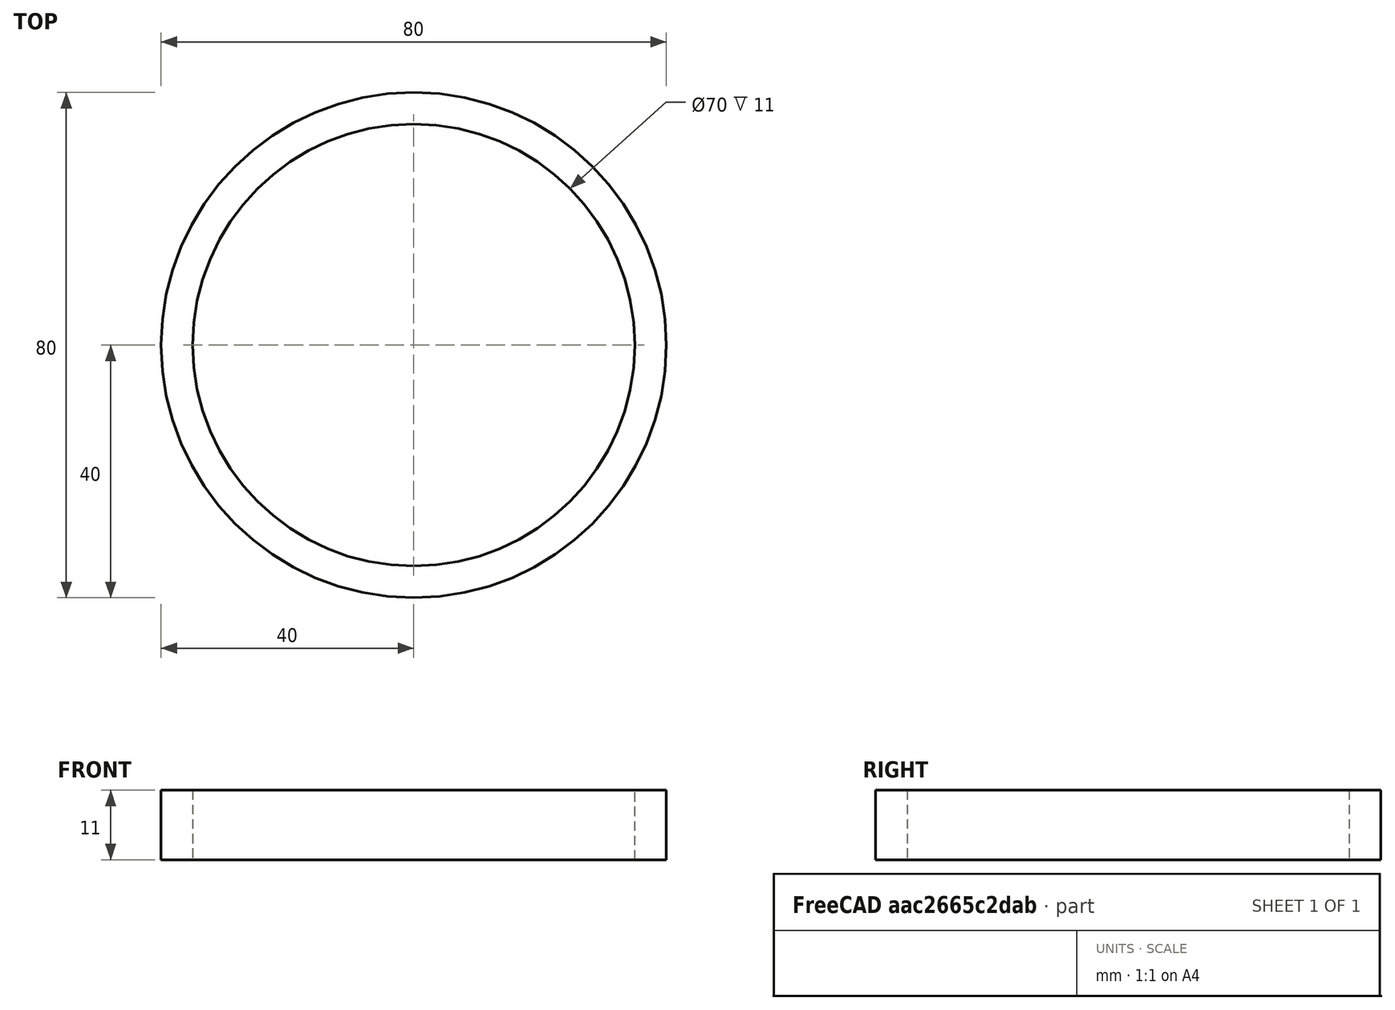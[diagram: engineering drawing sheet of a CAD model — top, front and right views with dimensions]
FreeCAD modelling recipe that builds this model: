
FCSTD DOCUMENT  (FreeCAD 0.19R24276 (Git))
Label: Ring_50x80x11_OUT
License: All rights reserved
LicenseURL: http://en.wikipedia.org/wiki/All_rights_reserved
objects: Sketcher::SketchObject×1, PartDesign::Pad×1, PartDesign::Body×1
note: 4 computed .brp shape members not serialized (recipe doc carries the construction recipe); baked Part::Feature solids carry a one-line shape summary decoded from their .brp

FEATURE [Sketcher::SketchObject] Sketch
  FullyConstrained = true
  MapMode = 5
  Support = -> [XY_Plane]
  sketch-geometry (2):
    g0: Circle CenterX=0 CenterY=0 CenterZ=0 NormalX=0 NormalY=0 NormalZ=1 AngleXU=0 Radius=35
    g1: Circle CenterX=0 CenterY=0 CenterZ=0 NormalX=0 NormalY=0 NormalZ=1 AngleXU=0 Radius=40
  constraints (4):
    c: Coincident(g1,g0)
    c: Diameter(g1) = 80
    c: Diameter(g0) = 70
    c: Coincident(g0,g-1)
FEATURE [PartDesign::Pad] Pad
  Direction = (1,1,1)
  Length = 11
  Length2 = 100
  Profile = -> Sketch
  Type = 0
FEATURE [PartDesign::Body] Body  label="Body_ring_out"
  Group = -> [Sketch,Pad]
  Origin = -> Origin
  Tip = -> Pad
